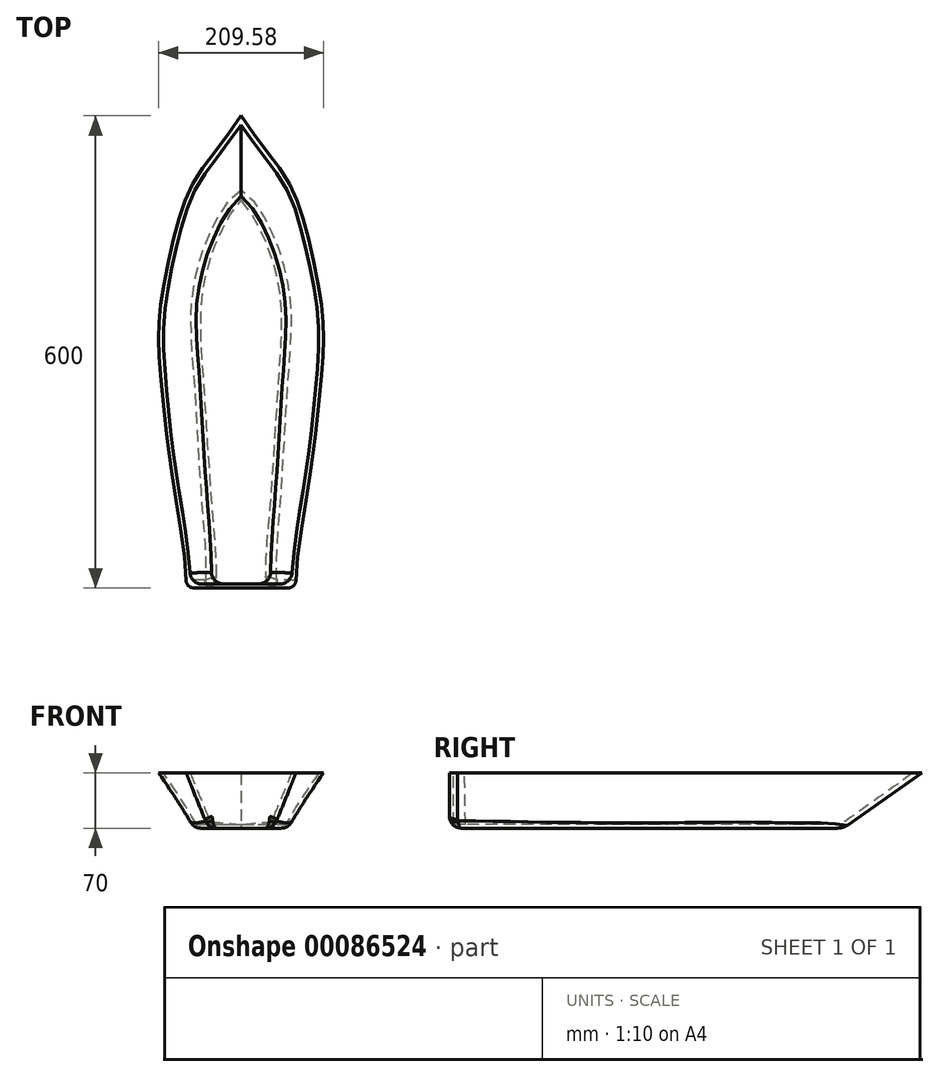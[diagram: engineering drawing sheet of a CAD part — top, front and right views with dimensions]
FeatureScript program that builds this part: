
annotation { "Feature Type Name" : "Feature", "Feature Type Description" : "" }
export const myFeature = defineFeature(function(context is Context, id is Id, definition is map)
    precondition{}
    {
        {
            var Q0;
            Q0=qCreatedBy(makeId("Front.planeOp"),FACE);
            cPlane(context, id + "F0", {"entities" : qUnion([Q0]), "cplaneType" : CPlaneType.OFFSET, "offset" : 100 * mm, "width" : 150 * mm, "height" : 150 * mm});
        }
        {
            var Q0;
            Q0=qCreatedBy(id+"F0.planeOp",FACE);
            cPlane(context, id + "F1", {"entities" : qUnion([Q0]), "cplaneType" : CPlaneType.OFFSET, "offset" : 100 * mm, "width" : 150 * mm, "height" : 150 * mm});
        }
        {
            var Q0;
            Q0=qCreatedBy(id+"F1.planeOp",FACE);
            cPlane(context, id + "F2", {"entities" : qUnion([Q0]), "cplaneType" : CPlaneType.OFFSET, "offset" : 100 * mm, "width" : 150 * mm, "height" : 150 * mm});
        }
        {
            var Q0;
            Q0=qCreatedBy(makeId("Front.planeOp"),FACE);
            cPlane(context, id + "F3", {"entities" : qUnion([Q0]), "cplaneType" : CPlaneType.OFFSET, "offset" : 100 * mm, "oppositeDirection" : true, "width" : 150 * mm, "height" : 150 * mm});
        }
        {
            var Q0;
            Q0=qCreatedBy(id+"F3.planeOp",FACE);
            cPlane(context, id + "F4", {"entities" : qUnion([Q0]), "cplaneType" : CPlaneType.OFFSET, "offset" : 100 * mm, "oppositeDirection" : true, "width" : 150 * mm, "height" : 150 * mm});
        }
        {
            var Q0;
            Q0=qCreatedBy(makeId("Top.planeOp"),FACE);
            cPlane(context, id + "F5", {"entities" : qUnion([Q0]), "cplaneType" : CPlaneType.OFFSET, "offset" : 70 * mm, "width" : 150 * mm, "height" : 150 * mm});
        }
        {
            var Q0;
            Q0=qCreatedBy(id+"F5.planeOp",FACE);
            var sketch = newSketch(context, id + "F6", { "sketchPlane" : qUnion([Q0])});
            skLineSegment(sketch, "E0", {"start": v(0, -300) * mm, "end": v(0, 300) * mm, "construction": true});
            skLineSegment(sketch, "E1", {"start": v(0, -300) * mm, "end": v(-70, -300) * mm});
            skFitSpline(sketch, "E2", {"points": [v(0, 300) * mm, v(-54.95, 224.5) * mm, v(-81.71, 158.41) * mm, v(-102.2, 58.66) * mm, v(-104.2, 0) * mm, v(-97.4, -79.6) * mm, v(-86.44, -163.21) * mm, v(-70, -300) * mm], "startDerivative": vector(-331.2, -540.25) * mm, "endDerivative": vector(-32.34, -483.7) * mm});
            skFitSpline(sketch, "E3.MirrorCS", {"points": [v(0, 300) * mm, v(54.95, 224.5) * mm, v(81.71, 158.41) * mm, v(102.2, 58.66) * mm, v(104.2, 0) * mm, v(97.4, -79.6) * mm, v(86.44, -163.21) * mm, v(70, -300) * mm], "startDerivative": vector(331.2, -540.25) * mm, "endDerivative": vector(32.34, -483.7) * mm});
            skLineSegment(sketch, "E4.MirrorCS", {"start": v(0, -300) * mm, "end": v(70, -300) * mm});
            skSolve(sketch);
        }
        {
            var Q0;
            Q0=qCreatedBy(makeId("Top.planeOp"),FACE);
            var sketch = newSketch(context, id + "F7", { "sketchPlane" : qUnion([Q0])});
            skLineSegment(sketch, "E5", {"start": v(0, -300) * mm, "end": v(0, 200) * mm, "construction": true});
            skLineSegment(sketch, "E6", {"start": v(0, -300) * mm, "end": v(-42.32, -300) * mm});
            skFitSpline(sketch, "E7", {"points": [v(0, 200) * mm, v(-37.48, 145.38) * mm, v(-52.98, 98.86) * mm, v(-59.77, 49.43) * mm, v(-54.92, -42.65) * mm, v(-50.08, -122.12) * mm, v(-44.26, -211.3) * mm, v(-42.32, -300) * mm], "startDerivative": vector(-362.9, -245.7) * mm, "endDerivative": vector(-58.16, -474.89) * mm});
            skFitSpline(sketch, "E8.MirrorCS", {"points": [v(0, 200) * mm, v(37.48, 145.38) * mm, v(52.98, 98.86) * mm, v(59.77, 49.43) * mm, v(54.92, -42.65) * mm, v(50.08, -122.12) * mm, v(44.26, -211.3) * mm, v(42.32, -300) * mm], "startDerivative": vector(362.9, -245.7) * mm, "endDerivative": vector(58.16, -474.89) * mm});
            skLineSegment(sketch, "E9.MirrorCS", {"start": v(0, -300) * mm, "end": v(42.32, -300) * mm});
            skSolve(sketch);
        }
        {
            var Q0;
            Q0=qCreatedBy(id+"F2.planeOp",FACE);
            var sketch = newSketch(context, id + "F8", { "sketchPlane" : qUnion([Q0])});
            skLineSegment(sketch, "E10", {"start": v(-70, 70) * mm, "end": v(-70, 10) * mm});
            skLineSegment(sketch, "E11", {"start": v(-60, 0) * mm, "end": v(-42.32, 0) * mm});
            skPoint(sketch, "E12.visualSharp", {"position": v(-70, 0) * mm});
            skArc(sketch, "E12.filletArc", {"start": v(-70, 10) * mm, "mid": v(-67.07, 2.93) * mm, "end": v(-60, 0) * mm});
            skSolve(sketch);
        }
        {
            var Q0;
            Q0=makeQuery(id+"F6.imprint","IMPRINT",FACE,{"disambiguationData":[TD([[makeQuery(id+"F6.imprint","IMPRINT",EDGE,{"derivedFrom":sQuery(id+"F6.wireOp",EDGE,"E1")}),-1.0]])]});
            var Q1;
            Q1=makeQuery(id+"F7.imprint","IMPRINT",FACE,{"disambiguationData":[TD([[makeQuery(id+"F7.imprint","IMPRINT",EDGE,{"derivedFrom":sQuery(id+"F7.wireOp",EDGE,"E6")}),-1.0]])]});
            var Q2;
            Q2=sQuery(id+"F8.wireOp",EDGE,"E12.filletArc");
            loft(context, id + "F9", {"sheetProfilesArray" : [{ "sheetProfileEntities" : qUnion([Q0]) }, { "sheetProfileEntities" : qUnion([Q1]) }], "guidesArray" : [{ "guideEntities" : qUnion([Q2]), "guideDerivativeType" : LoftGuideDerivativeType.DEFAULT, "guideDerivativeMagnitude" : 1 }]});
        }
        {
            var Q0;
            Q0=makeQuery(id+"F9.opLoft","CAP_FACE",FACE,{"disambiguationData":[OSD([makeQuery(id+"F6.imprint","IMPRINT",FACE,{"disambiguationData":[TD([[makeQuery(id+"F6.imprint","IMPRINT",EDGE,{"derivedFrom":sQuery(id+"F6.wireOp",EDGE,"E1")}),-1.0]])]})])],"isStart":true});
            shell(context, id + "F10", {"entities" : qUnion([Q0]), "thickness" : 5 * mm});
        }
        {
            var Q0;
            Q0=makeQuery(id+"F9.opLoft","MID_CAP_EDGE",EDGE,{"disambiguationData":[OSD([sQuery(id+"F7.wireOp",EDGE,"E6"),sQuery(id+"F7.wireOp",EDGE,"E8.MirrorCS"),sQuery(id+"F7.wireOp",EDGE,"E9.MirrorCS")])],"capPos":1.0});
            var Q1;
            Q1=makeQuery(id+"F9.opLoft","MID_CAP_EDGE",EDGE,{"disambiguationData":[OSD([sQuery(id+"F7.wireOp",EDGE,"E6"),sQuery(id+"F7.wireOp",EDGE,"E7"),sQuery(id+"F7.wireOp",EDGE,"E8.MirrorCS")])],"capPos":1.0});
            var Q2;
            Q2=makeQuery(id+"F9.opLoft","MID_CAP_EDGE",EDGE,{"disambiguationData":[OSD([sQuery(id+"F7.wireOp",EDGE,"E7"),sQuery(id+"F7.wireOp",EDGE,"E8.MirrorCS"),sQuery(id+"F7.wireOp",EDGE,"E9.MirrorCS")])],"capPos":1.0});
            fillet(context, id + "F11", {"entities" : qUnion([Q0, Q1, Q2]), "radius" : 15 * mm, "tangentPropagation" : true, "allowEdgeOverflow" : false});
        }
        {
            var Q0;
            Q0=makeQuery(id+"F9.opLoft","SWEPT_EDGE",EDGE,{"disambiguationData":[OSD([sQuery(id+"F6.wireOp",EDGE,"E1"),sQuery(id+"F6.wireOp",EDGE,"E2"),sQuery(id+"F7.wireOp",EDGE,"E6"),sQuery(id+"F7.wireOp",EDGE,"E7")])]});
            var Q1;
            Q1=makeQuery(id+"F9.opLoft","SWEPT_EDGE",EDGE,{"disambiguationData":[OSD([sQuery(id+"F6.wireOp",EDGE,"E3.MirrorCS"),sQuery(id+"F6.wireOp",EDGE,"E4.MirrorCS"),sQuery(id+"F7.wireOp",EDGE,"E8.MirrorCS"),sQuery(id+"F7.wireOp",EDGE,"E9.MirrorCS")])]});
            fillet(context, id + "F14", {"entities" : qUnion([Q0, Q1]), "radius" : 10 * mm, "tangentPropagation" : true, "allowEdgeOverflow" : false});
        }
        {
            var Q0;
            Q0=makeQuery(id+"F10.opShell","OFFSET_EDGE",EDGE,{"disambiguationData":[OSD([sQuery(id+"F6.wireOp",EDGE,"E3.MirrorCS"),sQuery(id+"F6.wireOp",EDGE,"E4.MirrorCS"),sQuery(id+"F7.wireOp",EDGE,"E8.MirrorCS"),sQuery(id+"F7.wireOp",EDGE,"E9.MirrorCS")])]});
            var Q1;
            Q1=makeQuery(id+"F10.opShell","OFFSET_EDGE",EDGE,{"disambiguationData":[OSD([sQuery(id+"F6.wireOp",EDGE,"E1"),sQuery(id+"F6.wireOp",EDGE,"E2"),sQuery(id+"F7.wireOp",EDGE,"E6"),sQuery(id+"F7.wireOp",EDGE,"E7")])]});
            fillet(context, id + "F12", {"entities" : qUnion([Q0, Q1]), "radius" : 15 * mm, "tangentPropagation" : true, "allowEdgeOverflow" : false});
        }
    });
